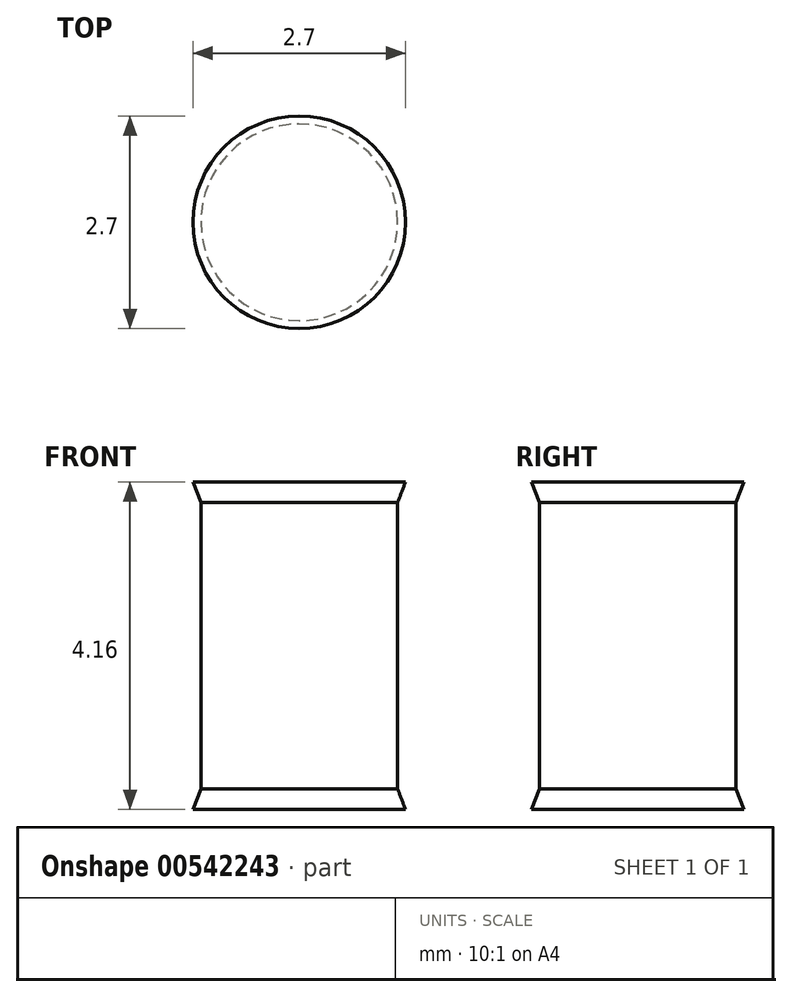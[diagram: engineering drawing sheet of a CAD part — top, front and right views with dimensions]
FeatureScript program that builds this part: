
annotation { "Feature Type Name" : "Feature", "Feature Type Description" : "" }
export const myFeature = defineFeature(function(context is Context, id is Id, definition is map)
    precondition{}
    {
        {
            var Q0;
            Q0=qCreatedBy(makeId("Front.planeOp"),FACE);
            var sketch = newSketch(context, id + "F0", { "sketchPlane" : qUnion([Q0])});
            skLineSegment(sketch, "E0", {"start": v(0, 0) * mm, "end": v(1.35, 0) * mm});
            skLineSegment(sketch, "E1", {"start": v(1.35, 0) * mm, "end": v(1.25, 0.26) * mm});
            skLineSegment(sketch, "E2", {"start": v(1.25, 0.26) * mm, "end": v(1.25, 3.9) * mm});
            skLineSegment(sketch, "E3", {"start": v(1.25, 3.9) * mm, "end": v(1.35, 4.16) * mm});
            skLineSegment(sketch, "E4", {"start": v(1.35, 4.16) * mm, "end": v(0, 4.16) * mm});
            skLineSegment(sketch, "E5", {"start": v(0, 4.16) * mm, "end": v(0, 0) * mm});
            skLineSegment(sketch, "E6", {"start": v(0, 4.55) * mm, "end": v(0, -0.32) * mm, "construction": true});
            skSolve(sketch);
        }
        {
            var Q0;
            Q0=makeQuery(id+"F0.imprint","IMPRINT",FACE,{"disambiguationData":[TD([[makeQuery(id+"F0.imprint","IMPRINT",EDGE,{"derivedFrom":sQuery(id+"F0.wireOp",EDGE,"E0")}),1.0]])]});
            var Q1;
            Q1=sQuery(id+"F0.wireOp",EDGE,"E6");
            revolve(context, id + "F1", {"surfaceOperationType" : NewSurfaceOperationType.NEW, "entities" : qUnion([Q0]), "axis" : qUnion([Q1]), "revolveType" : RevolveType.FULL});
        }
    });
